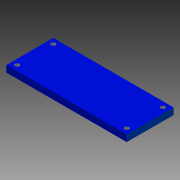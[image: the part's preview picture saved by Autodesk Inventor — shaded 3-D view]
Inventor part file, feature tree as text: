
AUTODESK INVENTOR PART (.ipt)
format: ipt  version: 2015 (Build 190159000, 159)  size: 103,936 bytes
history: native  units: mm
features: sketch x2, other x1, extrude x1, hole x1
ambient origin geometry x8: Origin, YZ Plane, XZ Plane, XY Plane, X Axis, Y Axis, Z Axis, Center Point
bodies: Body1 (feature_tree)
feature tree (5):
  other  "ソリッド1"
  extrude  "押し出し1"  Depth=90.0mm
  hole  "穴2"  [1 undecoded]
  sketch  "スケッチ1"
  sketch  "スケッチ3"
note: 1 required parameter value undecoded (feature->parameter linkage not recoverable at this tier; creation-order binding heuristic only, values carry confidence <= 0.55)
